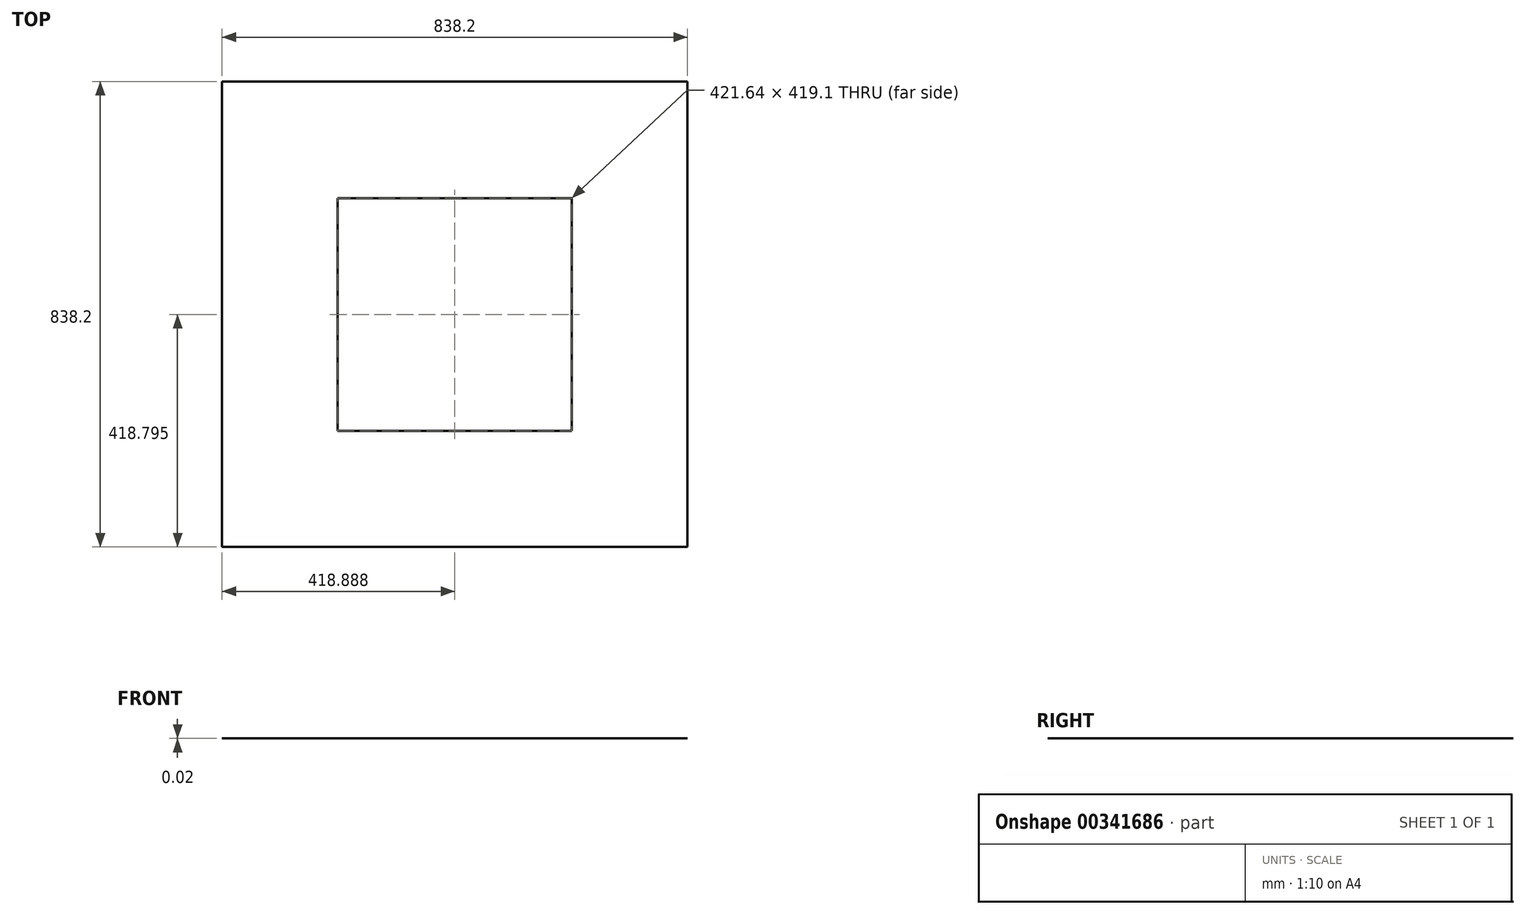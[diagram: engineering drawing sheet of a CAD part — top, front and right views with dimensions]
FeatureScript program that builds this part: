
annotation { "Feature Type Name" : "Feature", "Feature Type Description" : "" }
export const myFeature = defineFeature(function(context is Context, id is Id, definition is map)
    precondition{}
    {
        {
            var Q0;
            Q0=qCreatedBy(makeId("Top.planeOp"),FACE);
            var sketch = newSketch(context, id + "F0", { "sketchPlane" : qUnion([Q0])});
            skLineSegment(sketch, "E0.bottom", {"start": v(-427.16, 428.23) * mm, "end": v(411.04, 428.23) * mm});
            skLineSegment(sketch, "E0.top", {"start": v(-427.16, -409.97) * mm, "end": v(411.04, -409.97) * mm});
            skLineSegment(sketch, "E0.left", {"start": v(-427.16, 428.23) * mm, "end": v(-427.16, -409.97) * mm});
            skLineSegment(sketch, "E0.right", {"start": v(411.04, 428.23) * mm, "end": v(411.04, -409.97) * mm});
            skSolve(sketch);
        }
        {
            var Q0;
            Q0=makeQuery(id+"F0.imprint","IMPRINT",FACE,{"disambiguationData":[TD([[makeQuery(id+"F0.imprint","IMPRINT",EDGE,{"derivedFrom":sQuery(id+"F0.wireOp",EDGE,"E0.bottom")}),-1.0]])]});
            extrude(context, id + "F1", {"entities" : qUnion([Q0]), "depth" : 1 / 50.8 * mm});
        }
        {
            var Q0;
            Q0=makeQuery(id+"F1.opExtrude","CAP_FACE",FACE,{"disambiguationData":[OSD([sQuery(id+"F0.wireOp",EDGE,"E0.bottom"),sQuery(id+"F0.wireOp",EDGE,"E0.top"),sQuery(id+"F0.wireOp",EDGE,"E0.left"),sQuery(id+"F0.wireOp",EDGE,"E0.right")])],"isStart":false});
            var sketch = newSketch(context, id + "F2", { "sketchPlane" : qUnion([Q0])});
            skLineSegment(sketch, "E1.bottom", {"start": v(-219.1, 218.38) * mm, "end": v(202.55, 218.38) * mm});
            skLineSegment(sketch, "E1.top", {"start": v(-219.1, -200.72) * mm, "end": v(202.55, -200.72) * mm});
            skLineSegment(sketch, "E1.left", {"start": v(-219.1, 218.38) * mm, "end": v(-219.1, -200.72) * mm});
            skLineSegment(sketch, "E1.right", {"start": v(202.55, 218.38) * mm, "end": v(202.55, -200.72) * mm});
            skSolve(sketch);
        }
        {
            var Q0;
            Q0=makeQuery(id+"F2.imprint","IMPRINT",FACE,{"disambiguationData":[TD([[makeQuery(id+"F2.imprint","IMPRINT",EDGE,{"derivedFrom":sQuery(id+"F2.wireOp",EDGE,"E1.bottom")}),-1.0]])]});
            extrude(context, id + "F3", {"entities" : qUnion([Q0]), "operationType" : NewBodyOperationType.REMOVE, "oppositeDirection" : true, "depth" : 25.4 * mm, "offsetDistance" : 25.4 * mm});
        }
    });
